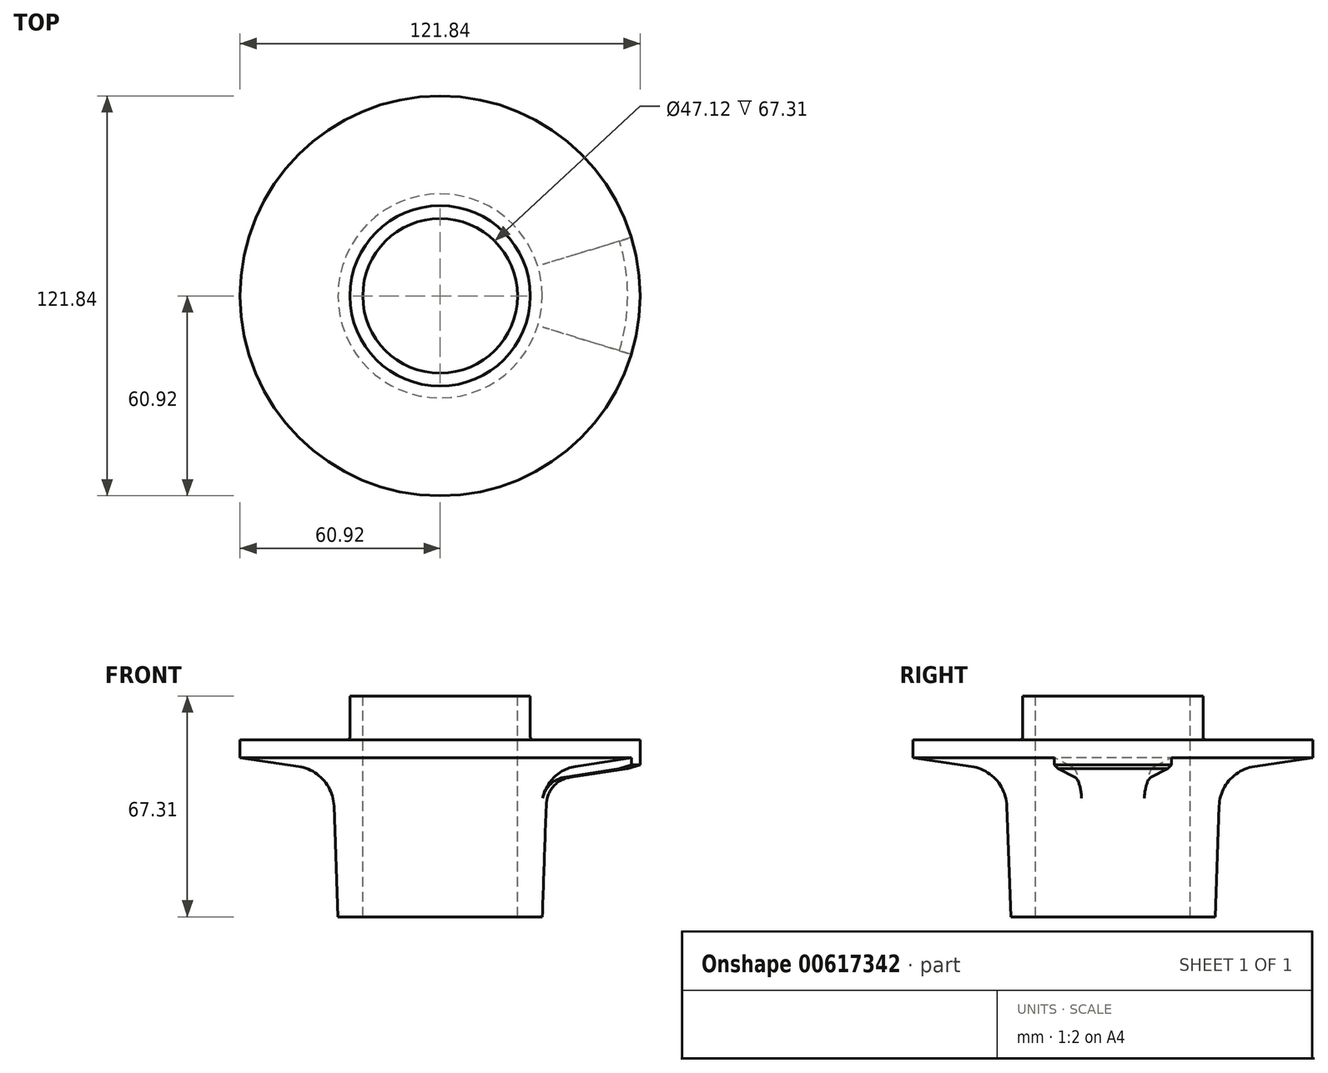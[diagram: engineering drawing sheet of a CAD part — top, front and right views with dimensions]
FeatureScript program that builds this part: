
annotation { "Feature Type Name" : "Feature", "Feature Type Description" : "" }
export const myFeature = defineFeature(function(context is Context, id is Id, definition is map)
    precondition{}
    {
        {
            var Q0;
            Q0=qCreatedBy(makeId("Front.planeOp"),FACE);
            var sketch = newSketch(context, id + "F0", { "sketchPlane" : qUnion([Q0])});
            skLineSegment(sketch, "E0", {"start": v(0, 0) * mm, "end": v(0, -67.31) * mm, "construction": true});
            skLineSegment(sketch, "E1", {"start": v(23.56, 0) * mm, "end": v(23.56, -67.31) * mm});
            skLineSegment(sketch, "E2", {"start": v(23.56, -67.31) * mm, "end": v(31.12, -67.31) * mm});
            skLineSegment(sketch, "E3", {"start": v(31.12, -67.31) * mm, "end": v(32.32, -33.6) * mm});
            skArc(sketch, "E4", {"start": v(43.11, -21.49) * mm, "mid": v(35.53, -25.6) * mm, "end": v(32.32, -33.6) * mm});
            skLineSegment(sketch, "E5", {"start": v(43.11, -21.49) * mm, "end": v(60.92, -18.8) * mm});
            skLineSegment(sketch, "E6", {"start": v(60.92, -18.8) * mm, "end": v(60.92, -13.34) * mm});
            skLineSegment(sketch, "E7", {"start": v(60.92, -13.34) * mm, "end": v(28.24, -13.34) * mm});
            skArc(sketch, "E8", {"start": v(27.48, -12.57) * mm, "mid": v(27.7, -13.11) * mm, "end": v(28.24, -13.34) * mm});
            skLineSegment(sketch, "E9", {"start": v(27.48, -12.57) * mm, "end": v(27.48, 0) * mm});
            skLineSegment(sketch, "E10", {"start": v(27.48, 0) * mm, "end": v(23.56, 0) * mm});
            skLineSegment(sketch, "E11.0.MirrorCS", {"start": v(-27.48, 0) * mm, "end": v(-23.56, 0) * mm, "construction": true});
            skArc(sketch, "E11.1.MirrorCS", {"start": v(-43.11, -21.49) * mm, "mid": v(-35.53, -25.6) * mm, "end": v(-32.32, -33.6) * mm, "construction": true});
            skLineSegment(sketch, "E11.2.MirrorCS", {"start": v(-27.48, -12.57) * mm, "end": v(-27.48, 0) * mm, "construction": true});
            skLineSegment(sketch, "E11.4.MirrorCS", {"start": v(-60.92, -13.33) * mm, "end": v(-28.24, -13.33) * mm, "construction": true});
            skLineSegment(sketch, "E11.6.MirrorCS", {"start": v(-27.48, 0) * mm, "end": v(-27.48, 0) * mm});
            skLineSegment(sketch, "E11.7.MirrorCS", {"start": v(-60.92, -18.8) * mm, "end": v(-60.92, -13.34) * mm, "construction": true});
            skLineSegment(sketch, "E11.8.MirrorCS", {"start": v(-27.48, 0) * mm, "end": v(-27.48, 0) * mm});
            skLineSegment(sketch, "E11.11.MirrorCS", {"start": v(-23.56, -67.31) * mm, "end": v(-31.11, -67.31) * mm, "construction": true});
            skLineSegment(sketch, "E11.19.MirrorCS", {"start": v(-43.11, -21.49) * mm, "end": v(-60.92, -18.8) * mm, "construction": true});
            skLineSegment(sketch, "E11.20.MirrorCS", {"start": v(-23.56, 0) * mm, "end": v(-23.56, -67.31) * mm, "construction": true});
            skLineSegment(sketch, "E11.25.MirrorCS", {"start": v(-31.12, -67.31) * mm, "end": v(-32.32, -33.6) * mm, "construction": true});
            skArc(sketch, "E11.27.MirrorCS", {"start": v(-27.48, -12.57) * mm, "mid": v(-27.7, -13.11) * mm, "end": v(-28.24, -13.33) * mm, "construction": true});
            skSolve(sketch);
        }
        {
            var Q0;
            Q0=makeQuery(id+"F0.imprint","IMPRINT",FACE,{"disambiguationData":[TD([[makeQuery(id+"F0.imprint","IMPRINT",EDGE,{"derivedFrom":sQuery(id+"F0.wireOp",EDGE,"E1")}),1.0]])]});
            var Q1;
            Q1=sQuery(id+"F0.wireOp",EDGE,"E0");
            revolve(context, id + "F1", {"entities" : qUnion([Q0]), "axis" : qUnion([Q1]), "revolveType" : RevolveType.FULL});
        }
        {
            var Q0;
            Q0=qCreatedBy(makeId("Front.planeOp"),FACE);
            var sketch = newSketch(context, id + "F2", { "sketchPlane" : qUnion([Q0])});
            skLineSegment(sketch, "E12.0", {"start": v(43.11, -21.49) * mm, "end": v(60.92, -18.8) * mm});
            skArc(sketch, "E12.1", {"start": v(43.11, -21.49) * mm, "mid": v(36.41, -24.7) * mm, "end": v(32.66, -31.12) * mm});
            skLineSegment(sketch, "E13", {"start": v(60.92, -18.8) * mm, "end": v(60.92, -20.96) * mm});
            skLineSegment(sketch, "E14", {"start": v(60.92, -20.96) * mm, "end": v(57.11, -22.17) * mm});
            skLineSegment(sketch, "E15", {"start": v(57.11, -22.17) * mm, "end": v(39.48, -24.83) * mm});
            skLineSegment(sketch, "E16", {"start": v(57.11, -22.17) * mm, "end": v(60.92, -21.6) * mm, "construction": true});
            skLineSegment(sketch, "E17", {"start": v(60.92, -21.6) * mm, "end": v(60.92, -20.96) * mm, "construction": true});
            skArc(sketch, "E18", {"start": v(39.48, -24.83) * mm, "mid": v(35.1, -26.93) * mm, "end": v(32.66, -31.12) * mm});
            skPoint(sketch, "E19.orphan", {"position": v(32.32, -33.6) * mm});
            skSolve(sketch);
        }
        {
            var Q0;
            Q0=makeQuery(id+"F2.imprint","IMPRINT",FACE,{"disambiguationData":[TD([[makeQuery(id+"F2.imprint","IMPRINT",EDGE,{"derivedFrom":sQuery(id+"F2.wireOp",EDGE,"E12.0")}),-1.0]])]});
            var Q1;
            Q1=sQuery(id+"F0.wireOp",EDGE,"E0");
            revolve(context, id + "F3", {"operationType" : NewBodyOperationType.ADD, "entities" : qUnion([Q0]), "axis" : qUnion([Q1]), "revolveType" : RevolveType.TWO_DIRECTIONS, "angle" : 17 * degree, "angleBack" : 343 * degree});
        }
        {
            var Q0;
            Q0=makeQuery(id+"F1.opRevolve","SWEPT_FACE",FACE,{"disambiguationData":[OSD([sQuery(id+"F0.wireOp",EDGE,"E7")])]});
            var sketch = newSketch(context, id + "F4", { "sketchPlane" : qUnion([Q0])});
            skCircle(sketch, "E20", {"center": v(50, 0) * mm, "radius": 6.3 * mm});
            skSolve(sketch);
        }
        {
            var Q0;
            Q0=makeQuery(id+"F1.opRevolve","SWEPT_FACE",FACE,{"disambiguationData":[OSD([sQuery(id+"F0.wireOp",EDGE,"E7")])]});
            cPlane(context, id + "F5", {"entities" : qUnion([Q0]), "cplaneType" : CPlaneType.OFFSET, "offset" : 7.92 * mm, "oppositeDirection" : true, "width" : 152.4 * mm, "height" : 152.4 * mm});
        }
    });
